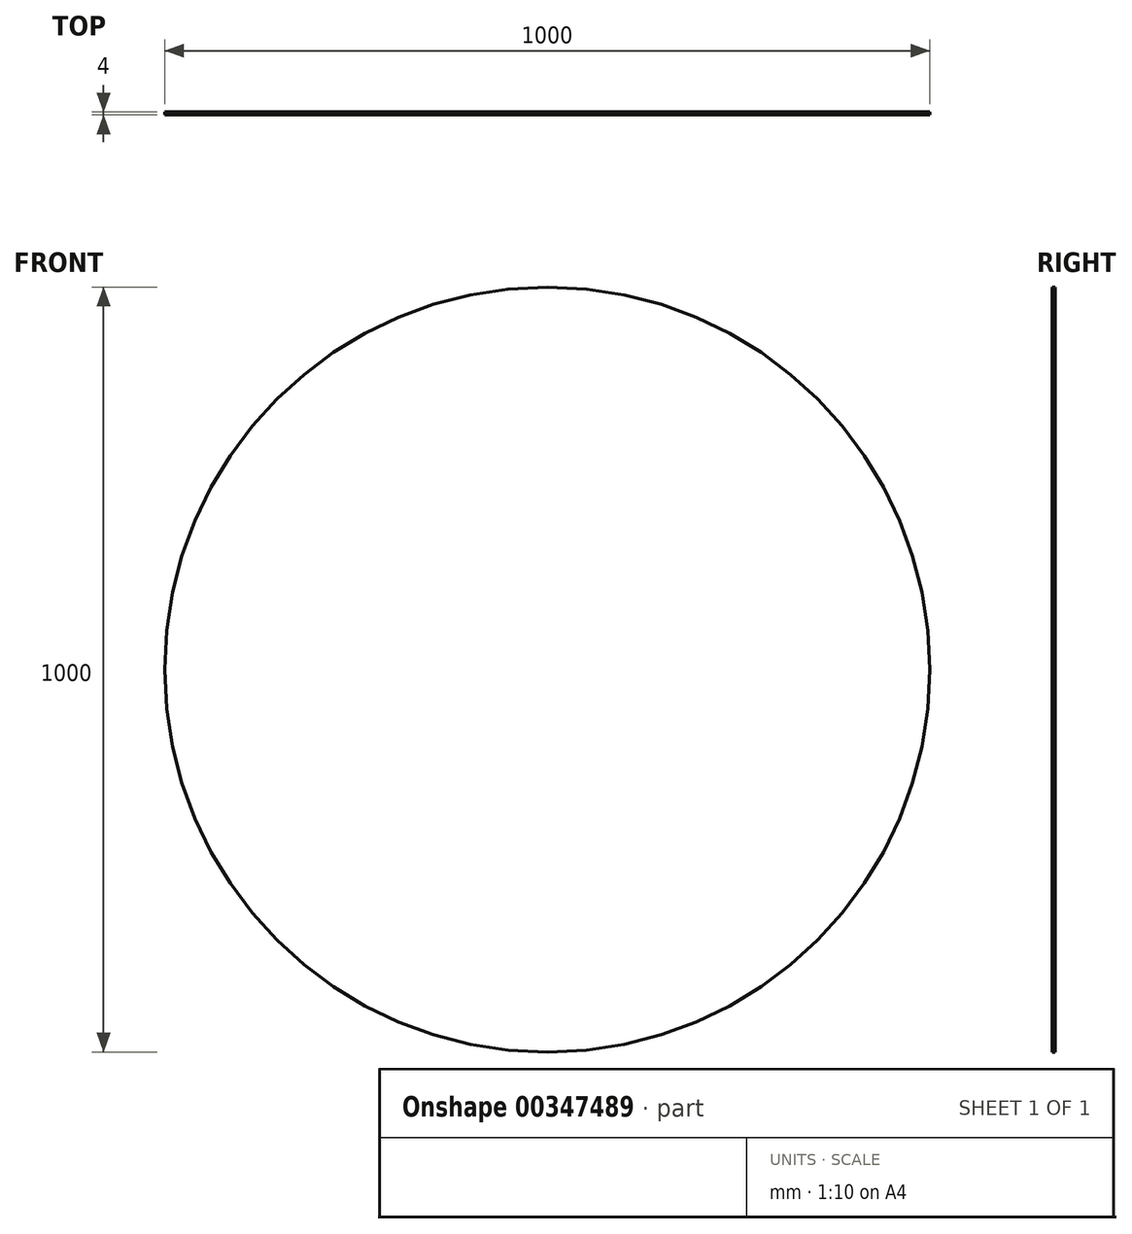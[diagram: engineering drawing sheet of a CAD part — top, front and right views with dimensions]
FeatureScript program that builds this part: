
annotation { "Feature Type Name" : "Feature", "Feature Type Description" : "" }
export const myFeature = defineFeature(function(context is Context, id is Id, definition is map)
    precondition{}
    {
        {
            var Q0;
            Q0=qCreatedBy(makeId("Front.planeOp"),FACE);
            var sketch = newSketch(context, id + "F0", { "sketchPlane" : qUnion([Q0])});
            skCircle(sketch, "E0", {"center": v(0, 0) * mm, "radius": 500 * mm});
            skSolve(sketch);
        }
        {
            var Q0;
            Q0 = qSketchRegion(id + "F0", true);
            extrude(context, id + "F1", {"entities" : qUnion([Q0]), "depth" : 4 * mm});
        }
    });
